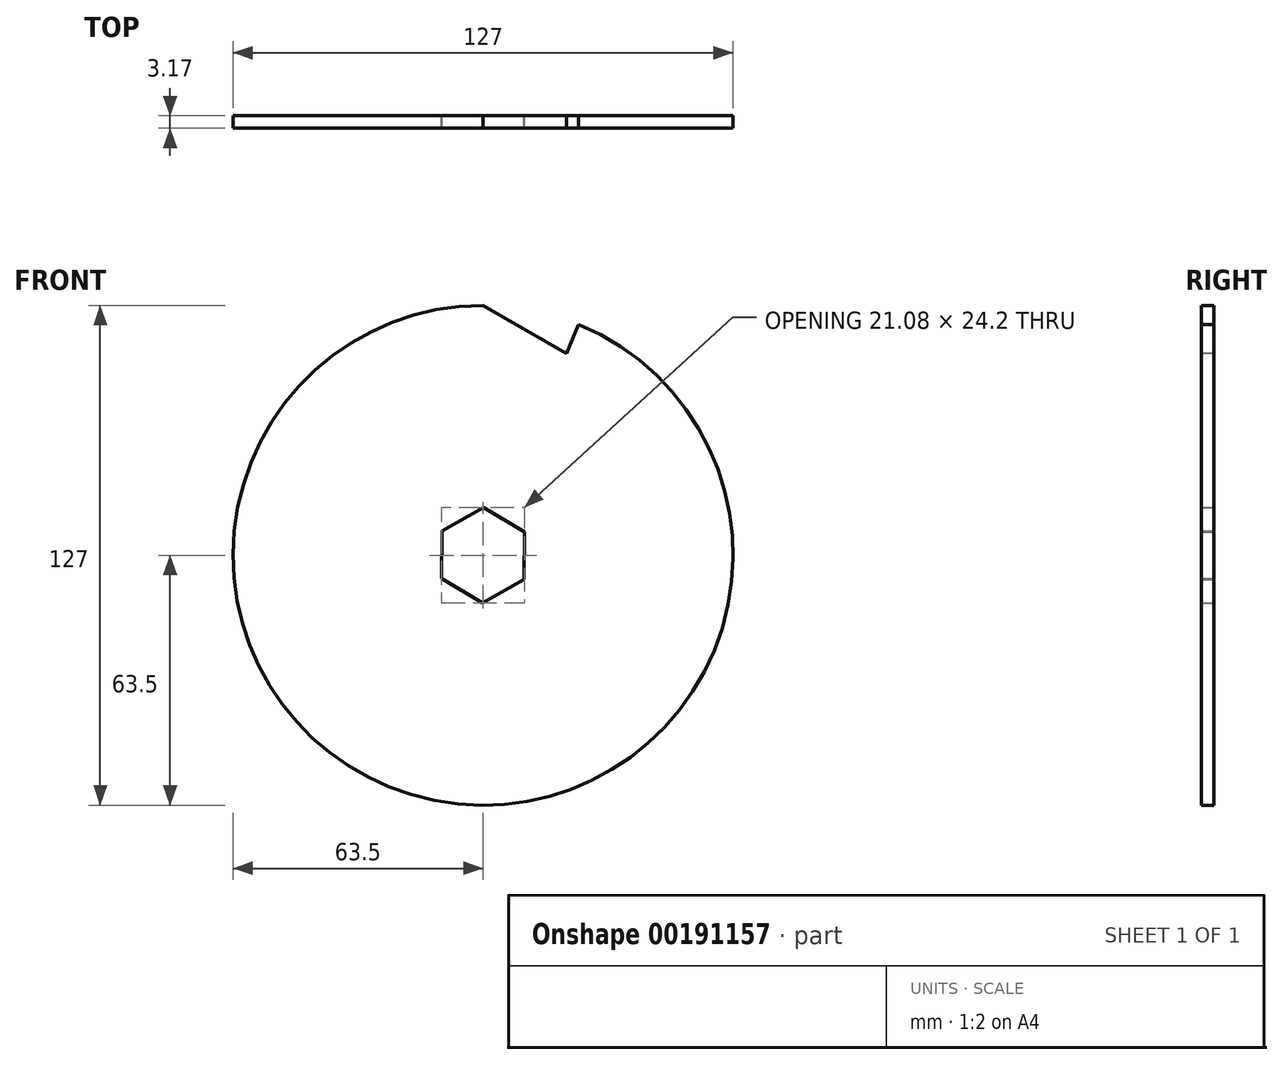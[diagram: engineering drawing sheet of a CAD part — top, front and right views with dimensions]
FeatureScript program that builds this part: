
annotation { "Feature Type Name" : "Feature", "Feature Type Description" : "" }
export const myFeature = defineFeature(function(context is Context, id is Id, definition is map)
    precondition{}
    {
        {
            var Q0;
            Q0=qCreatedBy(makeId("Front.planeOp"),FACE);
            var sketch = newSketch(context, id + "F0", { "sketchPlane" : qUnion([Q0])});
            skCircle(sketch, "E0", {"center": v(0, 0) * mm, "radius": 63.5 * mm});
            skSolve(sketch);
        }
        {
            var Q0;
            Q0 = qSketchRegion(id + "F0", true);
            extrude(context, id + "F1", {"entities" : qUnion([Q0]), "depth" : 3.17 * mm});
        }
        {
            var Q0;
            Q0=makeQuery(id+"F1.opExtrude","CAP_FACE",FACE,{"disambiguationData":[OSD([sQuery(id+"F0.wireOp",EDGE,"E0")])],"isStart":false});
            var sketch = newSketch(context, id + "F2", { "sketchPlane" : qUnion([Q0])});
            skLineSegment(sketch, "E1", {"start": v(21.23, 51.24) * mm, "end": v(24.3, 58.67) * mm});
            skLineSegment(sketch, "E2", {"start": v(0, 63.5) * mm, "end": v(21.23, 51.24) * mm});
            skArc(sketch, "E3", {"start": v(24.3, 58.67) * mm, "mid": v(12.39, 62.28) * mm, "end": v(0, 63.5) * mm});
            skSolve(sketch);
        }
        {
            var Q0;
            Q0 = qSketchRegion(id + "F2", true);
            extrude(context, id + "F3", {"entities" : qUnion([Q0]), "operationType" : NewBodyOperationType.REMOVE, "oppositeDirection" : true, "depth" : 3.17 * mm});
        }
        {
            var Q0;
            Q0=qCreatedBy(makeId("Front.planeOp"),FACE);
            var sketch = newSketch(context, id + "F4", { "sketchPlane" : qUnion([Q0])});
            skCircle(sketch, "E4.cCircle", {"center": v(0, 0) * mm, "radius": 10.48 * mm, "construction": true});
            skLineSegment(sketch, "E4.0", {"start": v(-10.41, 6.16) * mm, "end": v(0.13, 12.1) * mm});
            skLineSegment(sketch, "E4.1", {"start": v(0.13, 12.1) * mm, "end": v(10.54, 5.94) * mm});
            skLineSegment(sketch, "E4.2", {"start": v(10.54, 5.94) * mm, "end": v(10.41, -6.16) * mm});
            skLineSegment(sketch, "E4.3", {"start": v(10.41, -6.16) * mm, "end": v(-0.13, -12.1) * mm});
            skLineSegment(sketch, "E4.4", {"start": v(-0.13, -12.1) * mm, "end": v(-10.54, -5.94) * mm});
            skLineSegment(sketch, "E4.5", {"start": v(-10.54, -5.94) * mm, "end": v(-10.41, 6.16) * mm});
            skPoint(sketch, "E4.0.midPoint", {"position": v(-5.14, 9.13) * mm});
            skSolve(sketch);
        }
        {
            var Q0;
            Q0 = qSketchRegion(id + "F4", true);
            extrude(context, id + "F5", {"entities" : qUnion([Q0]), "operationType" : NewBodyOperationType.REMOVE, "depth" : 3.17 * mm});
        }
    });
